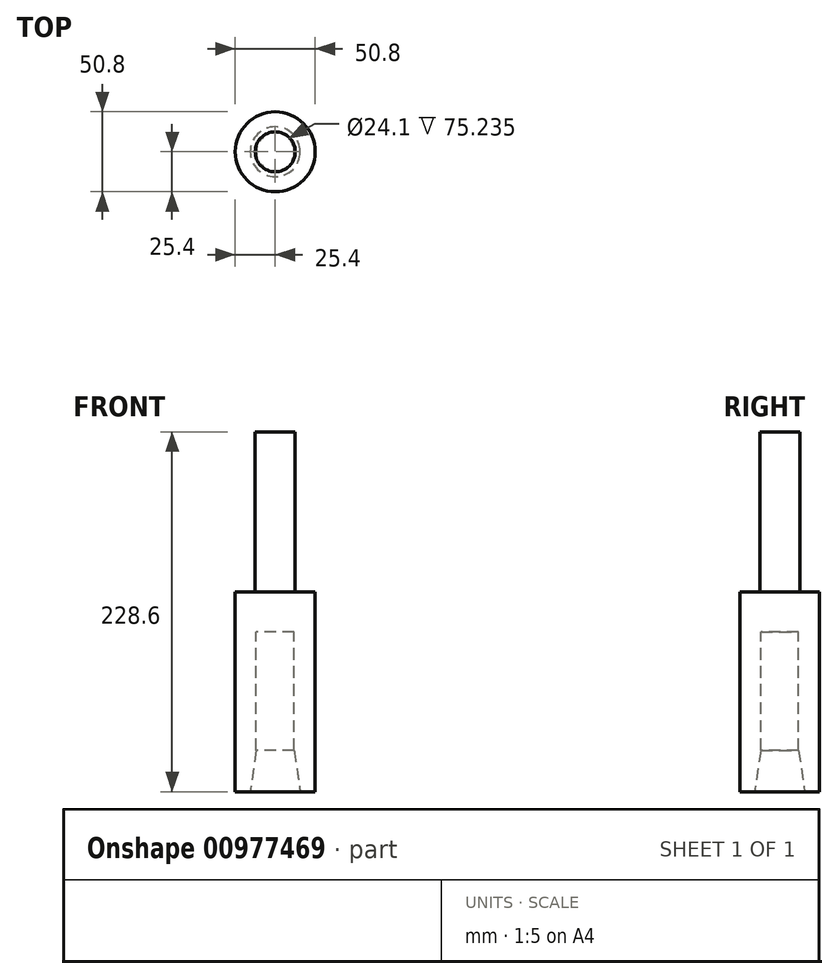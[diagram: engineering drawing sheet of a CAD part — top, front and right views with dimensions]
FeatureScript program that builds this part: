
annotation { "Feature Type Name" : "Feature", "Feature Type Description" : "" }
export const myFeature = defineFeature(function(context is Context, id is Id, definition is map)
    precondition{}
    {
        {
            var Q0;
            Q0=qCreatedBy(makeId("Front.planeOp"),FACE);
            var sketch = newSketch(context, id + "F0", { "sketchPlane" : qUnion([Q0])});
            skLineSegment(sketch, "E0", {"start": v(15.88, 0) * mm, "end": v(12.05, 26.36) * mm});
            skLineSegment(sketch, "E1", {"start": v(12.05, 26.36) * mm, "end": v(12.05, 101.6) * mm});
            skLineSegment(sketch, "E2", {"start": v(12.05, 101.6) * mm, "end": v(0, 101.6) * mm});
            skLineSegment(sketch, "E3", {"start": v(15.88, 0) * mm, "end": v(25.4, 0) * mm});
            skLineSegment(sketch, "E4", {"start": v(25.4, 0) * mm, "end": v(25.4, 127) * mm});
            skLineSegment(sketch, "E5", {"start": v(25.4, 127) * mm, "end": v(12.7, 127) * mm});
            skLineSegment(sketch, "E6", {"start": v(12.7, 127) * mm, "end": v(12.7, 228.6) * mm});
            skLineSegment(sketch, "E7", {"start": v(12.7, 228.6) * mm, "end": v(0, 228.6) * mm});
            skLineSegment(sketch, "E8", {"start": v(0, 228.6) * mm, "end": v(0, 101.6) * mm});
            skSolve(sketch);
        }
        {
            var Q0;
            Q0=makeQuery(id+"F0.imprint","IMPRINT",FACE,{"disambiguationData":[TD([[makeQuery(id+"F0.imprint","IMPRINT",EDGE,{"derivedFrom":sQuery(id+"F0.wireOp",EDGE,"E0")}),-1.0]])]});
            var Q1;
            Q1=sQuery(id+"F0.wireOp",EDGE,"E8");
            revolve(context, id + "F1", {"surfaceOperationType" : NewSurfaceOperationType.NEW, "entities" : qUnion([Q0]), "axis" : qUnion([Q1]), "revolveType" : RevolveType.FULL});
        }
    });
